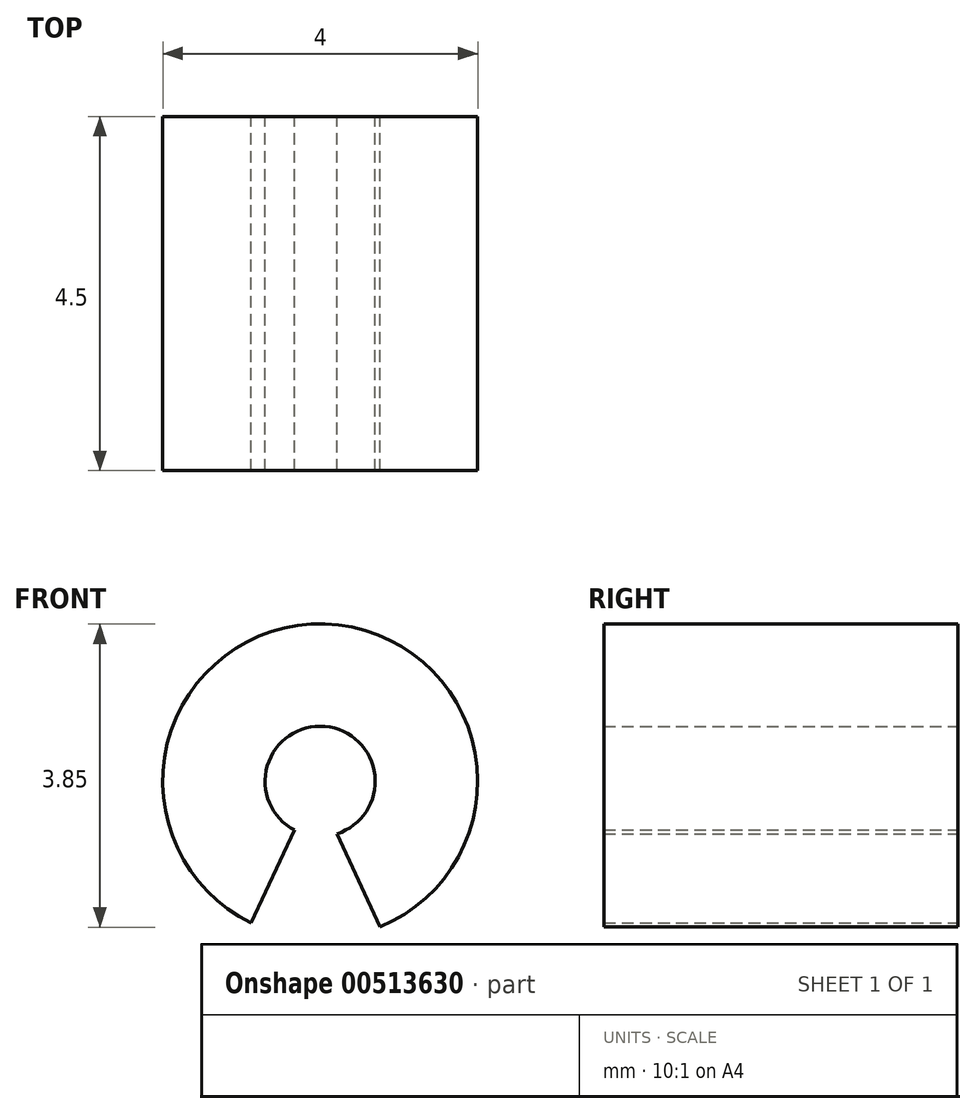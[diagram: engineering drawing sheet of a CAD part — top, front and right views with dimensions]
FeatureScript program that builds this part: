
annotation { "Feature Type Name" : "Feature", "Feature Type Description" : "" }
export const myFeature = defineFeature(function(context is Context, id is Id, definition is map)
    precondition{}
    {
        {
            var Q0;
            Q0=qCreatedBy(makeId("Front.planeOp"),FACE);
            var sketch = newSketch(context, id + "F0", { "sketchPlane" : qUnion([Q0])});
            skArc(sketch, "E0", {"start": v(-8.85, 4.3) * mm, "mid": v(-9.55, 8.14) * mm, "end": v(-10.49, 4.34) * mm});
            skArc(sketch, "E1", {"start": v(-9.4, 5.48) * mm, "mid": v(-9.55, 6.84) * mm, "end": v(-9.94, 5.52) * mm});
            skLineSegment(sketch, "E2", {"start": v(-9.61, 5.44) * mm, "end": v(-9.61, 2.58) * mm, "construction": true});
            skLineSegment(sketch, "E3", {"start": v(-9.4, 5.48) * mm, "end": v(-8.85, 4.3) * mm});
            skLineSegment(sketch, "E4", {"start": v(-9.94, 5.52) * mm, "end": v(-10.49, 4.34) * mm});
            skSolve(sketch);
        }
        {
            var Q0;
            Q0 = qSketchRegion(id + "F0", true);
            extrude(context, id + "F1", {"entities" : qUnion([Q0]), "depth" : 4.5 * mm, "offsetDistance" : 25 * mm});
        }
    });
